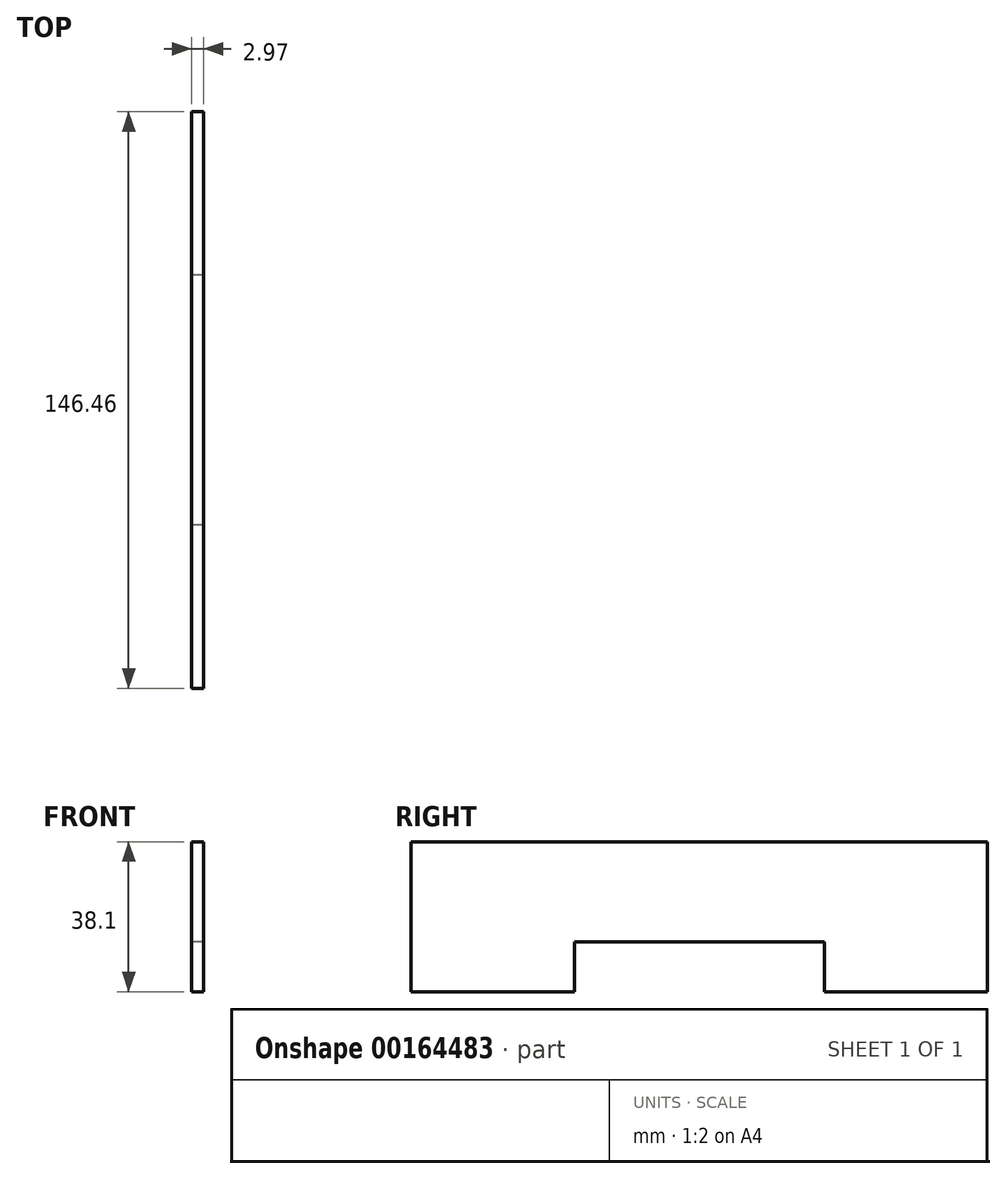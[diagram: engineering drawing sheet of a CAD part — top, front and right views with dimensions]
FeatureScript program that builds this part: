
annotation { "Feature Type Name" : "Feature", "Feature Type Description" : "" }
export const myFeature = defineFeature(function(context is Context, id is Id, definition is map)
    precondition{}
    {
        {
            var Q0;
            Q0=qCreatedBy(makeId("Right.planeOp"),FACE);
            var sketch = newSketch(context, id + "F0", { "sketchPlane" : qUnion([Q0])});
            skLineSegment(sketch, "E0.bottom", {"start": v(73.23, -19.05) * mm, "end": v(-73.23, -19.05) * mm});
            skLineSegment(sketch, "E0.top", {"start": v(73.23, 19.05) * mm, "end": v(-73.23, 19.05) * mm});
            skLineSegment(sketch, "E0.left", {"start": v(73.23, -19.05) * mm, "end": v(73.23, 19.05) * mm});
            skLineSegment(sketch, "E0.right", {"start": v(-73.23, -19.05) * mm, "end": v(-73.23, 19.05) * mm});
            skPoint(sketch, "E0.middle", {"position": v(0, 0) * mm});
            skLineSegment(sketch, "E1.bottom", {"start": v(-31.75, -6.35) * mm, "end": v(31.75, -6.35) * mm});
            skLineSegment(sketch, "E1.top", {"start": v(-31.75, -19.05) * mm, "end": v(31.75, -19.05) * mm});
            skLineSegment(sketch, "E1.left", {"start": v(-31.75, -6.35) * mm, "end": v(-31.75, -19.05) * mm});
            skLineSegment(sketch, "E1.right", {"start": v(31.75, -6.35) * mm, "end": v(31.75, -19.05) * mm});
            skSolve(sketch);
        }
        {
            var Q0;
            Q0=makeQuery(id+"F0.imprint","IMPRINT",FACE,{"disambiguationData":[TD([[makeQuery(id+"F0.imprint","IMPRINT",EDGE,{"derivedFrom":sQuery(id+"F0.wireOp",EDGE,"E0.top")}),1.0]])]});
            extrude(context, id + "F1", {"entities" : qUnion([Q0]), "depth" : 2.97 * mm});
        }
    });
